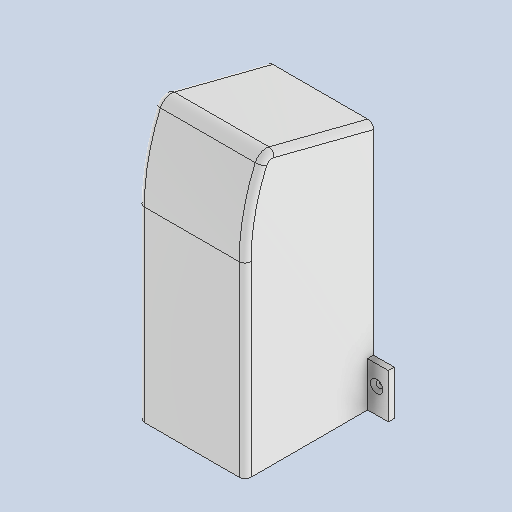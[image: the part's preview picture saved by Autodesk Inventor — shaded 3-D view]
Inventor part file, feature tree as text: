
AUTODESK INVENTOR PART (.ipt)
format: ipt  version: 2025 (Build 290162010, 162A)  size: 217,088 bytes
history: native  units: mm
features: other x7, extrude x6, sketch x6, reference x5, chamfer x2, projected_geometry x2, fillet x1
ambient origin geometry x8: Origin, YZ Plane, XZ Plane, XY Plane, X Axis, Y Axis, Z Axis, Center Point
bodies: Volumenkörper1 (feature_tree)
feature tree (29):
  extrude  "Extrusion1"  Depth=3.0mm
  extrude  "Extrusion2"  Depth=34.0mm TaperAngle=0.0deg
  extrude  "Extrusion3"  Depth=2.0mm
  sketch  "Skizze6"  dims[d20=15.0mm]
  fillet  "Rundung1"  Radius=7.0mm
  extrude  "Extrusion4"  Depth=7.0mm
  chamfer  "Fasen1"  Distance=2.2mm
  chamfer  "Fasen2"  Distance=2.0mm
  extrude  "Extrusion7"  Depth=1.0mm TaperAngle=45.0deg
  extrude  "Extrusion8"  Depth=1.0mm TaperAngle=45.0deg
  sketch  "Skizze1"  dims[d3=83.0mm d4=3.0mm]
  reference  "Referenz7"
  reference  "Referenz8"
  reference  "Referenz9"
  sketch  "Skizze2"  dims[d5=35.0mm d6=0.0mm d12=34.0mm d13=0.0mm]
  sketch  "Skizze3"  dims[d14=1.0mm d15=0.0mm d16=2.0mm d17=7.0mm]
  projected_geometry  "Projizierte Kontur2"
  sketch  "Skizze4"  dims[d18=15.0mm d19=7.0mm]
  reference  "Referenz10"
  reference  "Referenz11"
  projected_geometry  "Projizierte Kontur3"
  sketch  "Skizze8"  dims[d21=2.2mm d22=2.2mm d23=2.0mm d24=0.0mm d25=1.0mm d26=2.0mm d27=45.0deg d28=1.0mm d29=2.0mm d30=45.0deg d40=10.0mm d41=45.0deg d42=6.0mm d43=0.0mm d44=10.0mm d45=45.0deg d46=6.0mm d47=0.0mm]
  other  "<userpath>\GIT\HDVKBM\CAD\Krandemonstrator\Demonstrator.iam"
  other  "Demonstrator.iam"
  other  "Bedienhebel:1"
  other  "HebelhalterBlockBlind:1"
  other  "ISO 12633-2 - 20x20x2 - 200:1"
  other  "Schlitten:1"
  other  "SchlittenS:1"
